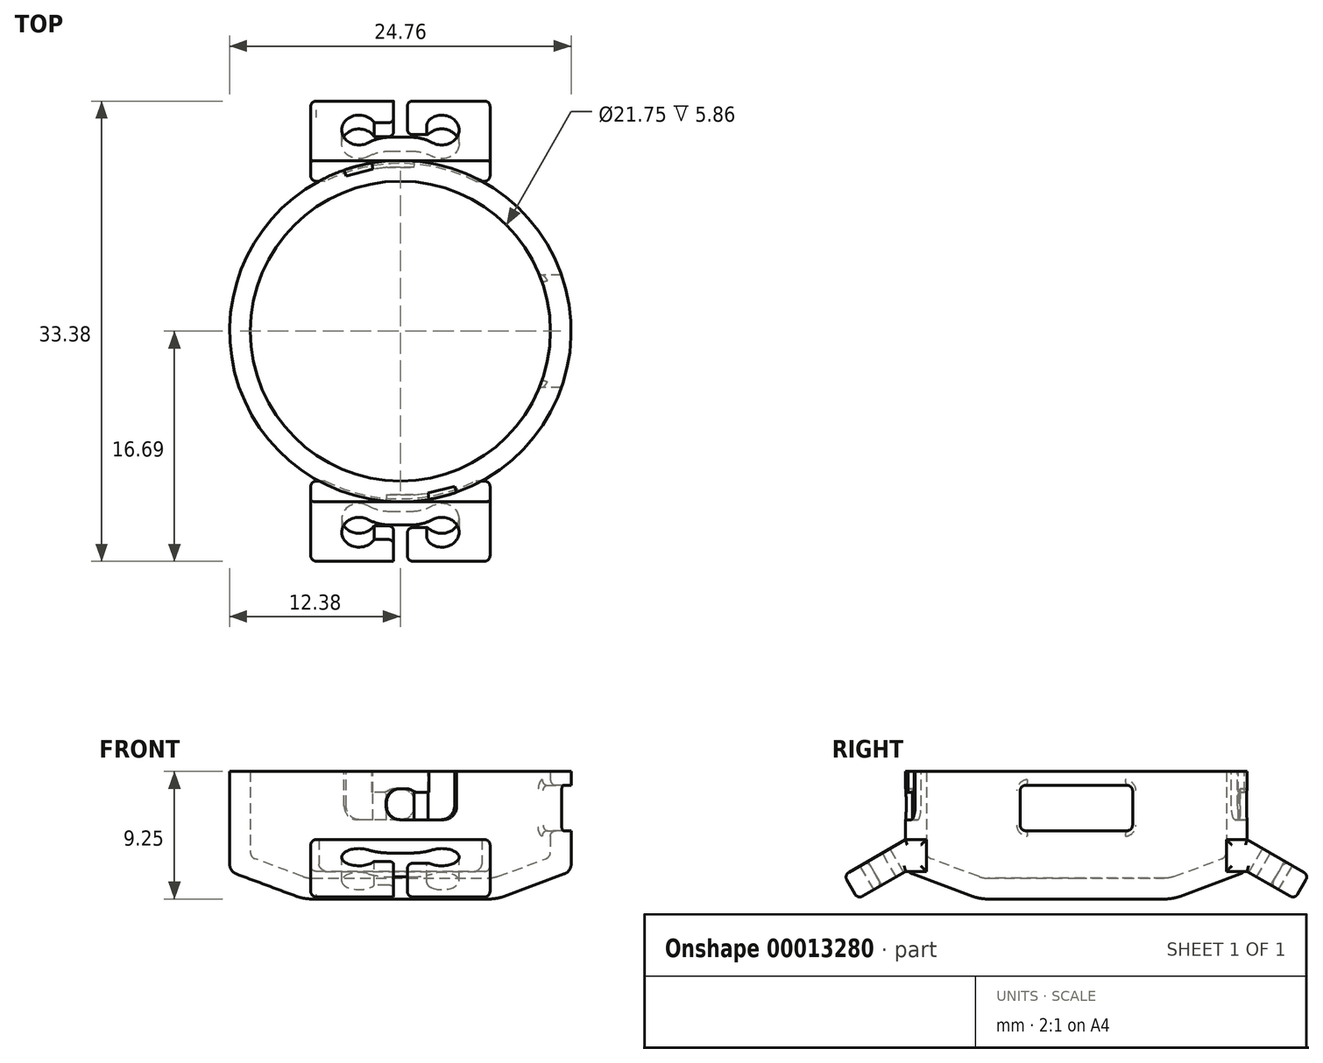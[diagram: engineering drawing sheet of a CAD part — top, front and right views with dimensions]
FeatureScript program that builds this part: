
annotation { "Feature Type Name" : "Feature", "Feature Type Description" : "" }
export const myFeature = defineFeature(function(context is Context, id is Id, definition is map)
    precondition{}
    {
        {
            var Q0;
            Q0=qCreatedBy(makeId("Front.planeOp"),FACE);
            var sketch = newSketch(context, id + "F0", { "sketchPlane" : qUnion([Q0])});
            skLineSegment(sketch, "E0", {"start": v(-12.38, 7.25) * mm, "end": v(-12.38, 0.52) * mm});
            skLineSegment(sketch, "E1", {"start": v(-11.89, -0.18) * mm, "end": v(-7.5, -1.81) * mm});
            skLineSegment(sketch, "E2", {"start": v(-6.46, -2) * mm, "end": v(0, -2) * mm});
            skLineSegment(sketch, "E3", {"start": v(0, -2) * mm, "end": v(0, -0.5) * mm});
            skLineSegment(sketch, "E4", {"start": v(0, -0.5) * mm, "end": v(-6.37, -0.5) * mm});
            skLineSegment(sketch, "E5", {"start": v(-7.07, -0.37) * mm, "end": v(-10.55, 0.92) * mm});
            skLineSegment(sketch, "E6", {"start": v(-10.88, 7.25) * mm, "end": v(-12.38, 7.25) * mm});
            skLineSegment(sketch, "E7", {"start": v(-10.88, 7.25) * mm, "end": v(-10.88, 1.39) * mm});
            skPoint(sketch, "E8.visualSharp", {"position": v(-12.38, 0) * mm});
            skArc(sketch, "E8.filletArc", {"start": v(-12.38, 0.52) * mm, "mid": v(-12.24, 0.1) * mm, "end": v(-11.89, -0.18) * mm});
            skPoint(sketch, "E9.visualSharp", {"position": v(-7, -2) * mm});
            skArc(sketch, "E9.filletArc", {"start": v(-7.5, -1.81) * mm, "mid": v(-7, -1.95) * mm, "end": v(-6.46, -2) * mm});
            skPoint(sketch, "E10.visualSharp", {"position": v(-10.88, 1.04) * mm});
            skArc(sketch, "E10.filletArc", {"start": v(-10.88, 1.39) * mm, "mid": v(-10.79, 1.1) * mm, "end": v(-10.55, 0.92) * mm});
            skPoint(sketch, "E11.visualSharp", {"position": v(-6.73, -0.5) * mm});
            skArc(sketch, "E11.filletArc", {"start": v(-7.07, -0.37) * mm, "mid": v(-6.72, -0.47) * mm, "end": v(-6.37, -0.5) * mm});
            skSolve(sketch);
        }
        {
            var Q0;
            Q0=makeQuery(id+"F0.imprint","IMPRINT",FACE,{"disambiguationData":[TD([[makeQuery(id+"F0.imprint","IMPRINT",EDGE,{"derivedFrom":sQuery(id+"F0.wireOp",EDGE,"E0")}),1.0]])]});
            var Q1;
            Q1=sQuery(id+"F0.wireOp",EDGE,"E3");
            revolve(context, id + "F1", {"entities" : qUnion([Q0]), "axis" : qUnion([Q1]), "revolveType" : RevolveType.FULL});
        }
        {
            var Q0;
            Q0=qCreatedBy(makeId("Right.planeOp"),FACE);
            var sketch = newSketch(context, id + "F2", { "sketchPlane" : qUnion([Q0])});
            skLineSegment(sketch, "E12", {"start": v(-10.88, 0) * mm, "end": v(-10.88, 2.3) * mm});
            skLineSegment(sketch, "E13", {"start": v(-10.88, 2.3) * mm, "end": v(-12.38, 2.3) * mm});
            skLineSegment(sketch, "E14", {"start": v(-12.38, 2.3) * mm, "end": v(-16.84, -0.27) * mm});
            skLineSegment(sketch, "E15", {"start": v(-16.84, -0.27) * mm, "end": v(-15.84, -2) * mm});
            skLineSegment(sketch, "E16", {"start": v(-15.84, -2) * mm, "end": v(-12.38, 0) * mm});
            skLineSegment(sketch, "E17", {"start": v(-12.38, 0) * mm, "end": v(-10.88, 0) * mm});
            skSolve(sketch);
        }
        {
            var Q0;
            Q0=makeQuery(id+"F2.imprint","IMPRINT",FACE,{"disambiguationData":[TD([[makeQuery(id+"F2.imprint","IMPRINT",EDGE,{"derivedFrom":sQuery(id+"F2.wireOp",EDGE,"E12")}),1.0]])]});
            extrude(context, id + "F3", {"entities" : qUnion([Q0]), "operationType" : NewBodyOperationType.ADD, "depth" : 6.5 * mm, "hasSecondDirection" : true, "secondDirectionOppositeDirection" : true, "secondDirectionDepth" : 6.5 * mm});
        }
        {
            var Q0;
            Q0=makeQuery(id+"F3.opExtrude","SWEPT_FACE",FACE,{"disambiguationData":[OSD([sQuery(id+"F2.wireOp",EDGE,"E14")])]});
            var sketch = newSketch(context, id + "F4", { "sketchPlane" : qUnion([Q0])});
            skLineSegment(sketch, "E18", {"start": v(-0.5, -14.72) * mm, "end": v(0.5, -14.72) * mm});
            skLineSegment(sketch, "E19", {"start": v(0.5, -14.72) * mm, "end": v(0.5, -12.72) * mm});
            skLineSegment(sketch, "E20", {"start": v(0.5, -12.72) * mm, "end": v(3, -12.72) * mm});
            skLineSegment(sketch, "E21", {"start": v(3, -12.72) * mm, "end": v(3, -11.52) * mm});
            skLineSegment(sketch, "E22", {"start": v(3, -11.52) * mm, "end": v(-3, -11.52) * mm});
            skLineSegment(sketch, "E23", {"start": v(-3, -11.52) * mm, "end": v(-3, -12.72) * mm});
            skLineSegment(sketch, "E24", {"start": v(-3, -12.72) * mm, "end": v(-0.5, -12.72) * mm});
            skLineSegment(sketch, "E25", {"start": v(-0.5, -12.72) * mm, "end": v(-0.5, -14.72) * mm});
            skCircle(sketch, "E26", {"center": v(-3, -12.12) * mm, "radius": 1.25 * mm});
            skCircle(sketch, "E27", {"center": v(3, -12.12) * mm, "radius": 1.25 * mm});
            skSolve(sketch);
        }
        {
            var Q0;
            {var subQ5=sQuery(id+"F4.wireOp",EDGE,"E23");Q0=makeQuery(id+"F4.imprint","IMPRINT",FACE,{"disambiguationData":[TD([[makeQuery(id+"F4.imprint","IMPRINT",EDGE,{"derivedFrom":subQ5}),-1.0]])]});}
            var Q1;
            {var subQ5=sQuery(id+"F4.wireOp",EDGE,"E23");Q1=makeQuery(id+"F4.imprint","IMPRINT",FACE,{"disambiguationData":[TD([[makeQuery(id+"F4.imprint","IMPRINT",EDGE,{"derivedFrom":subQ5}),1.0]])]});}
            var Q2;
            Q2=makeQuery(id+"F4.imprint","IMPRINT",FACE,{"disambiguationData":[TD([[makeQuery(id+"F4.imprint","IMPRINT",EDGE,{"derivedFrom":sQuery(id+"F4.wireOp",EDGE,"E18")}),-1.0]])]});
            var Q3;
            {var subQ5=sQuery(id+"F4.wireOp",EDGE,"E21");Q3=makeQuery(id+"F4.imprint","IMPRINT",FACE,{"disambiguationData":[TD([[makeQuery(id+"F4.imprint","IMPRINT",EDGE,{"derivedFrom":subQ5}),1.0]])]});}
            var Q4;
            {var subQ5=sQuery(id+"F4.wireOp",EDGE,"E21");Q4=makeQuery(id+"F4.imprint","IMPRINT",FACE,{"disambiguationData":[TD([[makeQuery(id+"F4.imprint","IMPRINT",EDGE,{"derivedFrom":subQ5}),-1.0]])]});}
            extrude(context, id + "F5", {"entities" : qUnion([Q0, Q1, Q2, Q3, Q4]), "operationType" : NewBodyOperationType.REMOVE, "endBound" : BoundingType.UP_TO_NEXT, "oppositeDirection" : true, "depth" : 25 * mm});
        }
        {
            var Q0;
            Q0=makeQuery(id+"F5.boolean.opBoolean","COPY",EDGE,{"derivedFrom":makeQuery(id+"F5.opExtrude","SWEPT_EDGE",EDGE,{"disambiguationData":[OSD([sQuery(id+"F4.wireOp",EDGE,"E22"),sQuery(id+"F4.wireOp",EDGE,"E26")])]})});
            var Q1;
            Q1=makeQuery(id+"F5.boolean.opBoolean","COPY",EDGE,{"derivedFrom":makeQuery(id+"F5.opExtrude","SWEPT_EDGE",EDGE,{"disambiguationData":[OSD([sQuery(id+"F4.wireOp",EDGE,"E22"),sQuery(id+"F4.wireOp",EDGE,"E27")])]})});
            fillet(context, id + "F6", {"entities" : qUnion([Q0, Q1]), "radius" : 3 * mm, "tangentPropagation" : true, "allowEdgeOverflow" : false});
        }
        {
            var Q0;
            Q0=makeQuery(id+"F5.boolean.opBoolean","COPY",EDGE,{"derivedFrom":makeQuery(id+"F5.opExtrude","SWEPT_EDGE",EDGE,{"disambiguationData":[OSD([sQuery(id+"F2.wireOp",EDGE,"E14"),sQuery(id+"F2.wireOp",EDGE,"E15"),sQuery(id+"F4.wireOp",EDGE,"E18"),sQuery(id+"F4.wireOp",EDGE,"E25")])]})});
            var Q1;
            Q1=makeQuery(id+"F5.boolean.opBoolean","COPY",EDGE,{"derivedFrom":makeQuery(id+"F5.opExtrude","SWEPT_EDGE",EDGE,{"disambiguationData":[OSD([sQuery(id+"F2.wireOp",EDGE,"E14"),sQuery(id+"F2.wireOp",EDGE,"E15"),sQuery(id+"F4.wireOp",EDGE,"E18"),sQuery(id+"F4.wireOp",EDGE,"E19")])]})});
            var Q2;
            Q2=makeQuery(id+"F5.boolean.opBoolean","COPY",EDGE,{"derivedFrom":makeQuery(id+"F5.opExtrude","SWEPT_EDGE",EDGE,{"disambiguationData":[OSD([sQuery(id+"F4.wireOp",EDGE,"E24"),sQuery(id+"F4.wireOp",EDGE,"E25")])]})});
            var Q3;
            Q3=makeQuery(id+"F5.boolean.opBoolean","COPY",EDGE,{"derivedFrom":makeQuery(id+"F5.opExtrude","SWEPT_EDGE",EDGE,{"disambiguationData":[OSD([sQuery(id+"F4.wireOp",EDGE,"E19"),sQuery(id+"F4.wireOp",EDGE,"E20")])]})});
            fillet(context, id + "F7", {"entities" : qUnion([Q0, Q1, Q2, Q3]), "radius" : .4 * mm, "tangentPropagation" : true, "allowEdgeOverflow" : false});
        }
        {
            var Q0;
            Q0=makeQuery(id+"F3.opExtrude","CAP_EDGE",EDGE,{"disambiguationData":[OSD([sQuery(id+"F2.wireOp",EDGE,"E13")])],"isStart":true});
            var Q1;
            Q1=makeQuery(id+"F3.opExtrude","CAP_EDGE",EDGE,{"disambiguationData":[OSD([sQuery(id+"F2.wireOp",EDGE,"E14")])],"isStart":true});
            var Q2;
            {var subQ0=sQuery(id+"F2.wireOp",EDGE,"E15");var subQ1=sQuery(id+"F2.wireOp",EDGE,"E14");Q2=makeQuery(id+"F5.boolean.opBoolean","SPLIT",EDGE,{"disambiguationData":[TD([makeQuery(id+"F5.opExtrude","SWEPT_FACE",FACE,{"disambiguationData":[OSD([sQuery(id+"F4.wireOp",EDGE,"E25")])]})])],"derivedFrom":makeQuery(id+"F3.opExtrude","SWEPT_EDGE",EDGE,{"disambiguationData":[OSD([subQ1,subQ0])]})});}
            var Q3;
            {var subQ0=sQuery(id+"F2.wireOp",EDGE,"E15");var subQ1=sQuery(id+"F2.wireOp",EDGE,"E14");Q3=makeQuery(id+"F5.boolean.opBoolean","SPLIT",EDGE,{"disambiguationData":[TD([makeQuery(id+"F5.opExtrude","SWEPT_FACE",FACE,{"disambiguationData":[OSD([sQuery(id+"F4.wireOp",EDGE,"E19")])]})])],"derivedFrom":makeQuery(id+"F3.opExtrude","SWEPT_EDGE",EDGE,{"disambiguationData":[OSD([subQ1,subQ0])]})});}
            var Q4;
            Q4=makeQuery(id+"F5.boolean.opBoolean","COPY",EDGE,{"derivedFrom":makeQuery(id+"F5.opExtrude","CAP_EDGE",EDGE,{"disambiguationData":[OSD([sQuery(id+"F4.wireOp",EDGE,"E27")])],"isStart":true})});
            var Q5;
            Q5=makeQuery(id+"F3.opExtrude","CAP_EDGE",EDGE,{"disambiguationData":[OSD([sQuery(id+"F2.wireOp",EDGE,"E14")])],"isStart":false});
            var Q6;
            Q6=makeQuery(id+"F3.opExtrude","CAP_EDGE",EDGE,{"disambiguationData":[OSD([sQuery(id+"F2.wireOp",EDGE,"E13")])],"isStart":false});
            var Q7;
            Q7=makeQuery(id+"F3.opExtrude","CAP_EDGE",EDGE,{"disambiguationData":[OSD([sQuery(id+"F2.wireOp",EDGE,"E12")])],"isStart":false});
            var Q8;
            Q8=makeQuery(id+"F3.opExtrude","CAP_EDGE",EDGE,{"disambiguationData":[OSD([sQuery(id+"F2.wireOp",EDGE,"E17")])],"isStart":false});
            var Q9;
            Q9=makeQuery(id+"F3.opExtrude","CAP_EDGE",EDGE,{"disambiguationData":[OSD([sQuery(id+"F2.wireOp",EDGE,"E16")])],"isStart":false});
            var Q10;
            Q10=makeQuery(id+"F3.opExtrude","CAP_EDGE",EDGE,{"disambiguationData":[OSD([sQuery(id+"F2.wireOp",EDGE,"E15")])],"isStart":false});
            var Q11;
            {var subQ0=sQuery(id+"F2.wireOp",EDGE,"E16");var subQ1=sQuery(id+"F2.wireOp",EDGE,"E15");Q11=makeQuery(id+"F5.boolean.opBoolean","SPLIT",EDGE,{"disambiguationData":[TD([makeQuery(id+"F5.opExtrude","SWEPT_FACE",FACE,{"disambiguationData":[OSD([sQuery(id+"F4.wireOp",EDGE,"E19")])]})])],"derivedFrom":makeQuery(id+"F3.opExtrude","SWEPT_EDGE",EDGE,{"disambiguationData":[OSD([subQ1,subQ0])]})});}
            var Q12;
            {var subQ0=sQuery(id+"F2.wireOp",EDGE,"E16");var subQ1=sQuery(id+"F2.wireOp",EDGE,"E15");Q12=makeQuery(id+"F5.boolean.opBoolean","SPLIT",EDGE,{"disambiguationData":[TD([makeQuery(id+"F5.opExtrude","SWEPT_FACE",FACE,{"disambiguationData":[OSD([sQuery(id+"F4.wireOp",EDGE,"E25")])]})])],"derivedFrom":makeQuery(id+"F3.opExtrude","SWEPT_EDGE",EDGE,{"disambiguationData":[OSD([subQ1,subQ0])]})});}
            var Q13;
            Q13=makeQuery(id+"F5.boolean.opBoolean","COPY",EDGE,{"derivedFrom":makeQuery(id+"F5.opExtrude","CAP_EDGE",EDGE,{"disambiguationData":[OSD([sQuery(id+"F4.wireOp",EDGE,"E26")])],"isStart":false})});
            var Q14;
            Q14=makeQuery(id+"F3.opExtrude","CAP_EDGE",EDGE,{"disambiguationData":[OSD([sQuery(id+"F2.wireOp",EDGE,"E15")])],"isStart":true});
            var Q15;
            Q15=makeQuery(id+"F3.opExtrude","CAP_EDGE",EDGE,{"disambiguationData":[OSD([sQuery(id+"F2.wireOp",EDGE,"E16")])],"isStart":true});
            var Q16;
            Q16=makeQuery(id+"F3.opExtrude","CAP_EDGE",EDGE,{"disambiguationData":[OSD([sQuery(id+"F2.wireOp",EDGE,"E17")])],"isStart":true});
            var Q17;
            Q17=makeQuery(id+"F3.opExtrude","CAP_EDGE",EDGE,{"disambiguationData":[OSD([sQuery(id+"F2.wireOp",EDGE,"E12")])],"isStart":true});
            fillet(context, id + "F8", {"entities" : qUnion([Q0, Q1, Q2, Q3, Q4, Q5, Q6, Q7, Q8, Q9, Q10, Q11, Q12, Q13, Q14, Q15, Q16, Q17]), "radius" : .4 * mm, "tangentPropagation" : true, "allowEdgeOverflow" : false});
        }
        {
            var Q0;
            Q0=makeQuery(id+"F1.opRevolve","SWEPT_BODY",BODY,{"disambiguationData":[OSD([sQuery(id+"F0.wireOp",EDGE,"E0"),sQuery(id+"F0.wireOp",EDGE,"E1"),sQuery(id+"F0.wireOp",EDGE,"E2"),sQuery(id+"F0.wireOp",EDGE,"E3"),sQuery(id+"F0.wireOp",EDGE,"E4"),sQuery(id+"F0.wireOp",EDGE,"E5"),sQuery(id+"F0.wireOp",EDGE,"E6"),sQuery(id+"F0.wireOp",EDGE,"E7"),sQuery(id+"F0.wireOp",EDGE,"E8.filletArc"),sQuery(id+"F0.wireOp",EDGE,"E9.filletArc"),sQuery(id+"F0.wireOp",EDGE,"E10.filletArc"),sQuery(id+"F0.wireOp",EDGE,"E11.filletArc")])]});
            var Q1;
            Q1=qCreatedBy(makeId("Front.planeOp"),FACE);
            mirror(context, id + "F9", {"operationType" : NewBodyOperationType.ADD, "entities" : qUnion([Q0]), "mirrorPlane" : qUnion([Q1])});
        }
        {
            var Q0;
            Q0=qCreatedBy(makeId("Right.planeOp"),FACE);
            var sketch = newSketch(context, id + "F10", { "sketchPlane" : qUnion([Q0])});
            skLineSegment(sketch, "E28.bottom", {"start": v(-3.68, 6.25) * mm, "end": v(3.68, 6.25) * mm});
            skLineSegment(sketch, "E28.top", {"start": v(-3.68, 2.95) * mm, "end": v(3.68, 2.95) * mm});
            skLineSegment(sketch, "E28.left", {"start": v(-4.08, 5.85) * mm, "end": v(-4.08, 3.35) * mm});
            skLineSegment(sketch, "E28.right", {"start": v(4.08, 5.85) * mm, "end": v(4.08, 3.35) * mm});
            skPoint(sketch, "E29.visualSharp", {"position": v(-4.08, 6.25) * mm});
            skArc(sketch, "E29.filletArc", {"start": v(-3.68, 6.25) * mm, "mid": v(-3.96, 6.13) * mm, "end": v(-4.08, 5.85) * mm});
            skPoint(sketch, "E30.visualSharp", {"position": v(4.08, 6.25) * mm});
            skArc(sketch, "E30.filletArc", {"start": v(4.08, 5.85) * mm, "mid": v(3.96, 6.13) * mm, "end": v(3.68, 6.25) * mm});
            skPoint(sketch, "E31.visualSharp", {"position": v(4.08, 2.95) * mm});
            skArc(sketch, "E31.filletArc", {"start": v(3.68, 2.95) * mm, "mid": v(3.96, 3.07) * mm, "end": v(4.08, 3.35) * mm});
            skPoint(sketch, "E32.visualSharp", {"position": v(-4.08, 2.95) * mm});
            skArc(sketch, "E32.filletArc", {"start": v(-4.08, 3.35) * mm, "mid": v(-3.96, 3.07) * mm, "end": v(-3.68, 2.95) * mm});
            skSolve(sketch);
        }
        {
            var Q0;
            Q0=qSketchRegion(id+"F10",true);
            var Q1;
            Q1=makeQuery(id+"F1.opRevolve","SWEPT_FACE",FACE,{"disambiguationData":[OSD([sQuery(id+"F0.wireOp",EDGE,"E0")])]});
            extrude(context, id + "F11", {"entities" : qUnion([Q0]), "operationType" : NewBodyOperationType.REMOVE, "endBound" : BoundingType.UP_TO_SURFACE, "endBoundEntityFace" : qUnion([Q1]), "depth" : 25 * mm});
        }
        {
            var Q0;
            Q0=makeQuery(id+"F11.boolean.opBoolean","COPY",EDGE,{"derivedFrom":makeQuery(id+"F11.opExtrude","CAP_EDGE",EDGE,{"disambiguationData":[OSD([sQuery(id+"F10.wireOp",EDGE,"E28.bottom")])],"isStart":false})});
            var Q1;
            Q1=makeQuery(id+"F11.boolean.opBoolean","INTERSECT",EDGE,{"derivedFrom":[makeQuery(id+"F1.opRevolve","SWEPT_FACE",FACE,{"disambiguationData":[OSD([sQuery(id+"F0.wireOp",EDGE,"E7")])]}),makeQuery(id+"F11.opExtrude","SWEPT_FACE",FACE,{"disambiguationData":[OSD([sQuery(id+"F10.wireOp",EDGE,"E28.top")])]})]});
            fillet(context, id + "F12", {"entities" : qUnion([Q0, Q1]), "radius" : .4 * mm, "tangentPropagation" : true, "allowEdgeOverflow" : false});
        }
        {
            var Q0;
            Q0=makeQuery(id+"F1.opRevolve","SWEPT_FACE",FACE,{"disambiguationData":[OSD([sQuery(id+"F0.wireOp",EDGE,"E6")])]});
            cPlane(context, id + "F13", {"entities" : qUnion([Q0]), "cplaneType" : CPlaneType.OFFSET, "offset" : 1.5 * mm, "oppositeDirection" : true, "width" : 150 * mm, "height" : 150 * mm});
        }
        {
            var Q0;
            Q0=qCreatedBy(id+"F13.planeOp",FACE);
            var sketch = newSketch(context, id + "F14", { "sketchPlane" : qUnion([Q0])});
            skLineSegment(sketch, "E33", {"start": v(0, 0) * mm, "end": v(0, -12.38) * mm, "construction": true});
            skCircle(sketch, "E34", {"center": v(0, 0) * mm, "radius": 12.38 * mm});
            skLineSegment(sketch, "E35", {"start": v(-1, -11.88) * mm, "end": v(1, -11.88) * mm});
            skLineSegment(sketch, "E36", {"start": v(0, 0) * mm, "end": v(-1.04, -12.33) * mm});
            skLineSegment(sketch, "E37", {"start": v(0, 0) * mm, "end": v(1.04, -12.33) * mm});
            skLineSegment(sketch, "E38", {"start": v(1, -11.88) * mm, "end": v(2, -11.75) * mm});
            skLineSegment(sketch, "E39", {"start": v(0, 0) * mm, "end": v(2.07, -12.2) * mm});
            skLineSegment(sketch, "E40", {"start": v(0, 0) * mm, "end": v(1.5, -11.81) * mm, "construction": true});
            skLineSegment(sketch, "E41", {"start": v(2, -11.75) * mm, "end": v(3.93, -11.25) * mm});
            skLineSegment(sketch, "E42", {"start": v(0, 0) * mm, "end": v(4.08, -11.68) * mm});
            skLineSegment(sketch, "E43", {"start": v(0, 0) * mm, "end": v(2.96, -11.5) * mm, "construction": true});
            skLineSegment(sketch, "E44.1.0", {"start": v(0, 0) * mm, "end": v(-4.08, 11.68) * mm});
            skLineSegment(sketch, "E44.1.1", {"start": v(-2, 11.75) * mm, "end": v(-3.93, 11.25) * mm});
            skLineSegment(sketch, "E44.1.2", {"start": v(0, 0) * mm, "end": v(-2.07, 12.2) * mm});
            skLineSegment(sketch, "E44.1.3", {"start": v(-1, 11.88) * mm, "end": v(-2, 11.75) * mm});
            skLineSegment(sketch, "E44.1.4", {"start": v(0, 0) * mm, "end": v(-1.04, 12.33) * mm});
            skLineSegment(sketch, "E44.1.5", {"start": v(1, 11.88) * mm, "end": v(-1, 11.88) * mm});
            skLineSegment(sketch, "E44.1.6", {"start": v(0, 0) * mm, "end": v(1.04, 12.33) * mm});
            skLineSegment(sketch, "E44.anchor1", {"start": v(0, 0) * mm, "end": v(4.08, -11.68) * mm, "construction": true});
            skLineSegment(sketch, "E44.anchor2", {"start": v(0, 0) * mm, "end": v(-4.08, 11.68) * mm, "construction": true});
            skSolve(sketch);
        }
        {
            var Q0;
            {var subQ3=sQuery(id+"F14.wireOp",EDGE,"E35");Q0=makeQuery(id+"F14.imprint","IMPRINT",FACE,{"disambiguationData":[TD([[makeQuery(id+"F14.imprint","IMPRINT",EDGE,{"derivedFrom":subQ3}),-1.0]])]});}
            var Q1;
            {var subQ3=sQuery(id+"F14.wireOp",EDGE,"E44.1.5");Q1=makeQuery(id+"F14.imprint","IMPRINT",FACE,{"disambiguationData":[TD([[makeQuery(id+"F14.imprint","IMPRINT",EDGE,{"derivedFrom":subQ3}),-1.0]])]});}
            extrude(context, id + "F15", {"entities" : qUnion([Q0, Q1]), "operationType" : NewBodyOperationType.REMOVE, "oppositeDirection" : true, "depth" : 2 * mm, "hasSecondDirection" : true, "secondDirectionOppositeDirection" : false, "secondDirectionDepth" : .25 * mm});
        }
        {
            var Q0;
            {var subQ3=sQuery(id+"F14.wireOp",EDGE,"E38");Q0=makeQuery(id+"F14.imprint","IMPRINT",FACE,{"disambiguationData":[TD([[makeQuery(id+"F14.imprint","IMPRINT",EDGE,{"derivedFrom":subQ3}),-1.0]])]});}
            var Q1;
            {var subQ3=sQuery(id+"F14.wireOp",EDGE,"E44.1.3");Q1=makeQuery(id+"F14.imprint","IMPRINT",FACE,{"disambiguationData":[TD([[makeQuery(id+"F14.imprint","IMPRINT",EDGE,{"derivedFrom":subQ3}),-1.0]])]});}
            extrude(context, id + "F16", {"entities" : qUnion([Q0, Q1]), "operationType" : NewBodyOperationType.REMOVE, "oppositeDirection" : true, "depth" : 2 * mm});
        }
        {
            var Q0;
            {var subQ3=sQuery(id+"F14.wireOp",EDGE,"E41");Q0=makeQuery(id+"F14.imprint","IMPRINT",FACE,{"disambiguationData":[TD([[makeQuery(id+"F14.imprint","IMPRINT",EDGE,{"derivedFrom":subQ3}),-1.0]])]});}
            var Q1;
            {var subQ3=sQuery(id+"F14.wireOp",EDGE,"E44.1.1");Q1=makeQuery(id+"F14.imprint","IMPRINT",FACE,{"disambiguationData":[TD([[makeQuery(id+"F14.imprint","IMPRINT",EDGE,{"derivedFrom":subQ3}),-1.0]])]});}
            extrude(context, id + "F17", {"entities" : qUnion([Q0, Q1]), "operationType" : NewBodyOperationType.REMOVE, "oppositeDirection" : true, "depth" : 2 * mm, "hasSecondDirection" : true, "secondDirectionBound" : SecondDirectionBoundingType.UP_TO_NEXT, "secondDirectionOppositeDirection" : false, "secondDirectionDepth" : 25 * mm});
        }
        {
            var Q0;
            Q0=makeQuery(id+"F15.boolean.opBoolean","COPY",EDGE,{"derivedFrom":makeQuery(id+"F15.opExtrude","CAP_EDGE",EDGE,{"disambiguationData":[OSD([sQuery(id+"F14.wireOp",EDGE,"E37")])],"isStart":true})});
            var Q1;
            Q1=makeQuery(id+"F15.boolean.opBoolean","COPY",EDGE,{"derivedFrom":makeQuery(id+"F15.opExtrude","CAP_EDGE",EDGE,{"disambiguationData":[OSD([sQuery(id+"F14.wireOp",EDGE,"E36")])],"isStart":true})});
            var Q2;
            Q2=makeQuery(id+"F15.boolean.opBoolean","COPY",EDGE,{"derivedFrom":makeQuery(id+"F15.opExtrude","CAP_EDGE",EDGE,{"disambiguationData":[OSD([sQuery(id+"F14.wireOp",EDGE,"E36")])],"isStart":false})});
            var Q3;
            Q3=makeQuery(id+"F17.boolean.opBoolean","COPY",EDGE,{"derivedFrom":makeQuery(id+"F17.opExtrude","CAP_EDGE",EDGE,{"disambiguationData":[OSD([sQuery(id+"F14.wireOp",EDGE,"E42")])],"isStart":false})});
            var Q4;
            Q4=makeQuery(id+"F15.boolean.opBoolean","COPY",EDGE,{"derivedFrom":makeQuery(id+"F15.opExtrude","CAP_EDGE",EDGE,{"disambiguationData":[OSD([sQuery(id+"F14.wireOp",EDGE,"E44.1.4")])],"isStart":true})});
            var Q5;
            Q5=makeQuery(id+"F15.boolean.opBoolean","COPY",EDGE,{"derivedFrom":makeQuery(id+"F15.opExtrude","CAP_EDGE",EDGE,{"disambiguationData":[OSD([sQuery(id+"F14.wireOp",EDGE,"E44.1.6")])],"isStart":true})});
            var Q6;
            Q6=makeQuery(id+"F15.boolean.opBoolean","COPY",EDGE,{"derivedFrom":makeQuery(id+"F15.opExtrude","CAP_EDGE",EDGE,{"disambiguationData":[OSD([sQuery(id+"F14.wireOp",EDGE,"E44.1.6")])],"isStart":false})});
            var Q7;
            Q7=makeQuery(id+"F17.boolean.opBoolean","COPY",EDGE,{"derivedFrom":makeQuery(id+"F17.opExtrude","CAP_EDGE",EDGE,{"disambiguationData":[OSD([sQuery(id+"F14.wireOp",EDGE,"E44.1.0")])],"isStart":false})});
            fillet(context, id + "F18", {"entities" : qUnion([Q0, Q1, Q2, Q3, Q4, Q5, Q6, Q7]), "radius" : 1 * mm, "tangentPropagation" : true, "allowEdgeOverflow" : false});
        }
        {
            var Q0;
            Q0=makeQuery(id+"F16.boolean.opBoolean","COPY",EDGE,{"derivedFrom":makeQuery(id+"F16.opExtrude","CAP_EDGE",EDGE,{"disambiguationData":[OSD([sQuery(id+"F14.wireOp",EDGE,"E37")])],"isStart":true})});
            var Q1;
            Q1=makeQuery(id+"F16.boolean.opBoolean","COPY",EDGE,{"derivedFrom":makeQuery(id+"F16.opExtrude","CAP_EDGE",EDGE,{"disambiguationData":[OSD([sQuery(id+"F14.wireOp",EDGE,"E39")])],"isStart":true})});
            var Q2;
            Q2=makeQuery(id+"F16.boolean.opBoolean","COPY",EDGE,{"derivedFrom":makeQuery(id+"F16.opExtrude","CAP_EDGE",EDGE,{"disambiguationData":[OSD([sQuery(id+"F14.wireOp",EDGE,"E44.1.2")])],"isStart":true})});
            var Q3;
            Q3=makeQuery(id+"F16.boolean.opBoolean","COPY",EDGE,{"derivedFrom":makeQuery(id+"F16.opExtrude","CAP_EDGE",EDGE,{"disambiguationData":[OSD([sQuery(id+"F14.wireOp",EDGE,"E44.1.4")])],"isStart":true})});
            var Q4;
            {var subQ0=sQuery(id+"F14.wireOp",EDGE,"E37");Q4=makeQuery(id+"F18.opFillet","BLEND_EDGE",EDGE,{"blendedFrom":[makeQuery(id+"F15.boolean.opBoolean","COPY",EDGE,{"derivedFrom":makeQuery(id+"F15.opExtrude","CAP_EDGE",EDGE,{"disambiguationData":[OSD([subQ0])],"isStart":true})}),makeQuery(id+"F16.boolean.opBoolean","COPY",FACE,{"derivedFrom":makeQuery(id+"F16.opExtrude","CAP_FACE",FACE,{"disambiguationData":[OSD([sQuery(id+"F14.wireOp",EDGE,"E34"),subQ0,sQuery(id+"F14.wireOp",EDGE,"E38"),sQuery(id+"F14.wireOp",EDGE,"E39")])],"isStart":true})})],"blendedInto":[makeQuery(id+"F16.boolean.opBoolean","COPY",FACE,{"derivedFrom":makeQuery(id+"F16.opExtrude","CAP_FACE",FACE,{"disambiguationData":[OSD([sQuery(id+"F14.wireOp",EDGE,"E34"),subQ0,sQuery(id+"F14.wireOp",EDGE,"E38"),sQuery(id+"F14.wireOp",EDGE,"E39")])],"isStart":true})})]});}
            var Q5;
            {var subQ0=sQuery(id+"F14.wireOp",EDGE,"E44.1.4");Q5=makeQuery(id+"F18.opFillet","BLEND_EDGE",EDGE,{"blendedFrom":[makeQuery(id+"F15.boolean.opBoolean","COPY",EDGE,{"derivedFrom":makeQuery(id+"F15.opExtrude","CAP_EDGE",EDGE,{"disambiguationData":[OSD([subQ0])],"isStart":true})}),makeQuery(id+"F16.boolean.opBoolean","COPY",FACE,{"derivedFrom":makeQuery(id+"F16.opExtrude","CAP_FACE",FACE,{"disambiguationData":[OSD([sQuery(id+"F14.wireOp",EDGE,"E34"),sQuery(id+"F14.wireOp",EDGE,"E44.1.2"),sQuery(id+"F14.wireOp",EDGE,"E44.1.3"),subQ0])],"isStart":true})})],"blendedInto":[makeQuery(id+"F16.boolean.opBoolean","COPY",FACE,{"derivedFrom":makeQuery(id+"F16.opExtrude","CAP_FACE",FACE,{"disambiguationData":[OSD([sQuery(id+"F14.wireOp",EDGE,"E34"),sQuery(id+"F14.wireOp",EDGE,"E44.1.2"),sQuery(id+"F14.wireOp",EDGE,"E44.1.3"),subQ0])],"isStart":true})})]});}
            fillet(context, id + "F19", {"entities" : qUnion([Q0, Q1, Q2, Q3, Q4, Q5]), "radius" : .25 * mm, "tangentPropagation" : true, "allowEdgeOverflow" : false});
        }
    });
